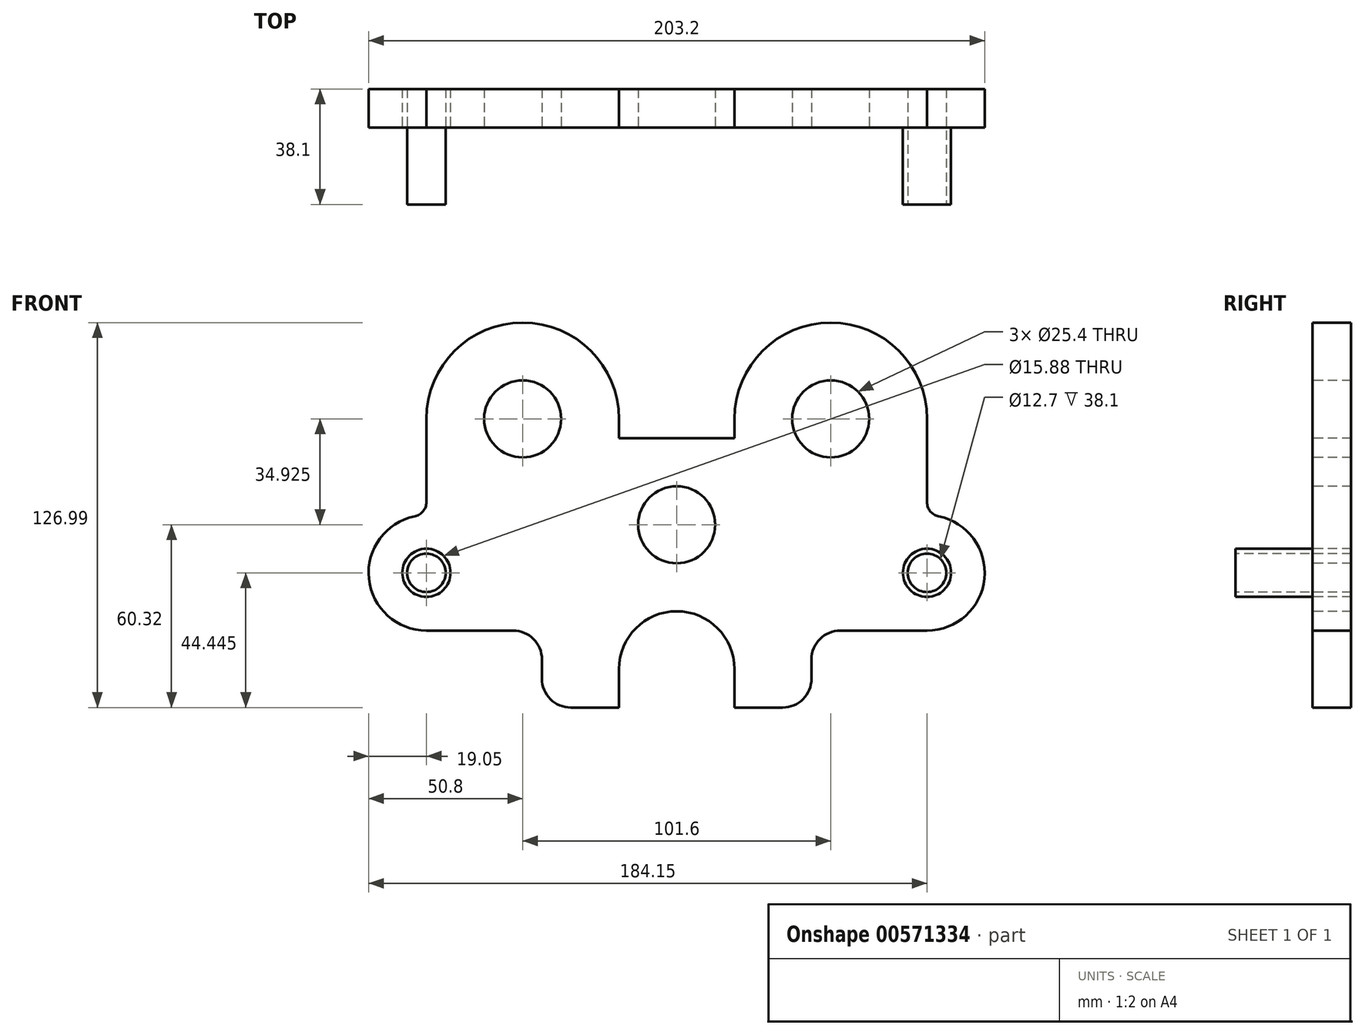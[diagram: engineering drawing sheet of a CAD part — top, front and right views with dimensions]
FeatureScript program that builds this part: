
annotation { "Feature Type Name" : "Feature", "Feature Type Description" : "" }
export const myFeature = defineFeature(function(context is Context, id is Id, definition is map)
    precondition{}
    {
        {
            var Q0;
            Q0=qCreatedBy(makeId("Front.planeOp"),FACE);
            var sketch = newSketch(context, id + "F0", { "sketchPlane" : qUnion([Q0])});
            skLineSegment(sketch, "E0", {"start": v(50.8, 46.36) * mm, "end": v(50.8, 0) * mm, "construction": true});
            skLineSegment(sketch, "E1", {"start": v(0, 34.93) * mm, "end": v(62.77, 34.93) * mm, "construction": true});
            skLineSegment(sketch, "E2", {"start": v(0, 47.1) * mm, "end": v(0, -90.6) * mm, "construction": true});
            skLineSegment(sketch, "E3", {"start": v(0, 0) * mm, "end": v(100.31, 0) * mm, "construction": true});
            skLineSegment(sketch, "E4.MirrorCS", {"start": v(0, 34.93) * mm, "end": v(-62.77, 34.93) * mm, "construction": true});
            skLineSegment(sketch, "E5.MirrorCS", {"start": v(0, 0) * mm, "end": v(-100.31, 0) * mm, "construction": true});
            skCircle(sketch, "E6", {"center": v(50.8, 34.93) * mm, "radius": 12.7 * mm});
            skCircle(sketch, "E7", {"center": v(0, 0) * mm, "radius": 12.7 * mm});
            skPoint(sketch, "E8.startSnap0", {"position": v(31.38, 34.93) * mm});
            skLineSegment(sketch, "E9", {"start": v(19.05, 28.57) * mm, "end": v(19.05, 34.93) * mm});
            skArc(sketch, "E10", {"start": v(82.55, 34.93) * mm, "mid": v(50.8, 66.68) * mm, "end": v(19.05, 34.93) * mm});
            skLineSegment(sketch, "E11", {"start": v(82.55, 34.93) * mm, "end": v(82.55, 7.46) * mm});
            skLineSegment(sketch, "E12", {"start": v(70.06, -15.88) * mm, "end": v(102.63, -15.88) * mm, "construction": true});
            skLineSegment(sketch, "E13", {"start": v(82.55, -9.84) * mm, "end": v(82.55, -41.13) * mm, "construction": true});
            skPoint(sketch, "E14", {"position": v(82.55, -15.87) * mm});
            skCircle(sketch, "E15", {"center": v(82.55, -15.87) * mm, "radius": 6.35 * mm});
            skLineSegment(sketch, "E16", {"start": v(19.05, 28.57) * mm, "end": v(-23.18, 28.57) * mm});
            skArc(sketch, "E17", {"start": v(82.55, -34.92) * mm, "mid": v(101.5, -17.79) * mm, "end": v(86.36, 2.8) * mm});
            skLineSegment(sketch, "E18", {"start": v(82.55, -34.92) * mm, "end": v(53.98, -34.92) * mm});
            skLineSegment(sketch, "E19", {"start": v(44.45, -44.45) * mm, "end": v(44.45, -50.8) * mm});
            skLineSegment(sketch, "E20", {"start": v(34.93, -60.32) * mm, "end": v(19.05, -60.32) * mm});
            skLineSegment(sketch, "E21", {"start": v(19.05, -60.32) * mm, "end": v(19.05, -47.62) * mm});
            skLineSegment(sketch, "E22", {"start": v(-32.06, -47.62) * mm, "end": v(27.67, -47.62) * mm, "construction": true});
            skArc(sketch, "E23", {"start": v(19.05, -47.62) * mm, "mid": v(0, -28.57) * mm, "end": v(-19.05, -47.63) * mm});
            skLineSegment(sketch, "E24.MirrorCS", {"start": v(-19.05, 28.57) * mm, "end": v(-19.05, 34.92) * mm});
            skArc(sketch, "E25.MirrorCS", {"start": v(-82.55, 34.92) * mm, "mid": v(-50.8, 66.68) * mm, "end": v(-19.05, 34.92) * mm});
            skLineSegment(sketch, "E26.MirrorCS", {"start": v(-82.55, 34.92) * mm, "end": v(-82.55, 7.46) * mm});
            skArc(sketch, "E27.MirrorCS", {"start": v(-82.55, -34.92) * mm, "mid": v(-101.5, -17.79) * mm, "end": v(-86.36, 2.8) * mm});
            skCircle(sketch, "E28.MirrorC", {"center": v(-82.55, -15.87) * mm, "radius": 6.35 * mm});
            skCircle(sketch, "E29.MirrorC", {"center": v(-50.8, 34.93) * mm, "radius": 12.7 * mm});
            skLineSegment(sketch, "E30.MirrorCS", {"start": v(-82.55, -34.93) * mm, "end": v(-53.97, -34.92) * mm});
            skLineSegment(sketch, "E31.MirrorCS", {"start": v(-44.45, -44.45) * mm, "end": v(-44.45, -50.8) * mm});
            skLineSegment(sketch, "E32.MirrorCS", {"start": v(-34.93, -60.32) * mm, "end": v(-19.05, -60.32) * mm});
            skLineSegment(sketch, "E33.MirrorCS", {"start": v(-19.05, -60.33) * mm, "end": v(-19.05, -47.63) * mm});
            skLineSegment(sketch, "E34.MirrorCS", {"start": v(-82.55, -9.84) * mm, "end": v(-82.55, -41.13) * mm, "construction": true});
            skLineSegment(sketch, "E35.MirrorCS", {"start": v(-50.8, 46.36) * mm, "end": v(-50.8, 0) * mm, "construction": true});
            skLineSegment(sketch, "E36.MirrorCS", {"start": v(-70.06, -15.88) * mm, "end": v(-102.63, -15.88) * mm, "construction": true});
            skPoint(sketch, "E37.visualSharp", {"position": v(-82.55, 3.17) * mm});
            skArc(sketch, "E37.filletArc", {"start": v(-86.36, 2.8) * mm, "mid": v(-83.62, 4.44) * mm, "end": v(-82.55, 7.46) * mm});
            skPoint(sketch, "E38.visualSharp", {"position": v(82.55, 3.17) * mm});
            skArc(sketch, "E38.filletArc", {"start": v(82.55, 7.46) * mm, "mid": v(83.62, 4.44) * mm, "end": v(86.36, 2.8) * mm});
            skPoint(sketch, "E39.visualSharp", {"position": v(-44.45, -34.92) * mm});
            skArc(sketch, "E39.filletArc", {"start": v(-44.45, -44.45) * mm, "mid": v(-47.24, -37.71) * mm, "end": v(-53.97, -34.92) * mm});
            skPoint(sketch, "E40.visualSharp", {"position": v(44.45, -34.92) * mm});
            skArc(sketch, "E40.filletArc", {"start": v(53.98, -34.92) * mm, "mid": v(47.24, -37.71) * mm, "end": v(44.45, -44.45) * mm});
            skPoint(sketch, "E41.visualSharp", {"position": v(-44.45, -60.32) * mm});
            skArc(sketch, "E41.filletArc", {"start": v(-44.45, -50.8) * mm, "mid": v(-41.66, -57.54) * mm, "end": v(-34.93, -60.32) * mm});
            skPoint(sketch, "E42.visualSharp", {"position": v(44.45, -60.32) * mm});
            skArc(sketch, "E42.filletArc", {"start": v(34.93, -60.32) * mm, "mid": v(41.66, -57.54) * mm, "end": v(44.45, -50.8) * mm});
            skCircle(sketch, "E43", {"center": v(82.55, -15.87) * mm, "radius": 7.94 * mm});
            skCircle(sketch, "E44.MirrorC", {"center": v(-82.55, -15.87) * mm, "radius": 7.94 * mm});
            skSolve(sketch);
        }
        {
            var Q0;
            Q0 = qSketchRegion(id + "F0", true);
            var Q1;
            Q1=makeQuery(id+"F0.imprint","IMPRINT",FACE,{"disambiguationData":[TD([[makeQuery(id+"F0.imprint","IMPRINT",EDGE,{"derivedFrom":sQuery(id+"F0.wireOp",EDGE,"E15")}),-1.0]])]});
            var Q2;
            Q2=makeQuery(id+"F0.imprint","IMPRINT",FACE,{"disambiguationData":[TD([[makeQuery(id+"F0.imprint","IMPRINT",EDGE,{"derivedFrom":sQuery(id+"F0.wireOp",EDGE,"E28.MirrorC")}),1.0]])]});
            extrude(context, id + "F1", {"entities" : qUnion([Q0, Q1, Q2]), "oppositeDirection" : true, "depth" : 12.7 * mm, "offsetDistance" : 25.4 * mm});
        }
        {
            var Q0;
            Q0=makeQuery(id+"F0.imprint","IMPRINT",FACE,{"disambiguationData":[TD([[makeQuery(id+"F0.imprint","IMPRINT",EDGE,{"derivedFrom":sQuery(id+"F0.wireOp",EDGE,"E28.MirrorC")}),1.0]])]});
            var Q1;
            Q1=makeQuery(id+"F0.imprint","IMPRINT",FACE,{"disambiguationData":[TD([[makeQuery(id+"F0.imprint","IMPRINT",EDGE,{"derivedFrom":sQuery(id+"F0.wireOp",EDGE,"E15")}),-1.0]])]});
            extrude(context, id + "F2", {"entities" : qUnion([Q0, Q1]), "operationType" : NewBodyOperationType.ADD, "depth" : 25.4 * mm, "offsetDistance" : 25.4 * mm});
        }
    });
